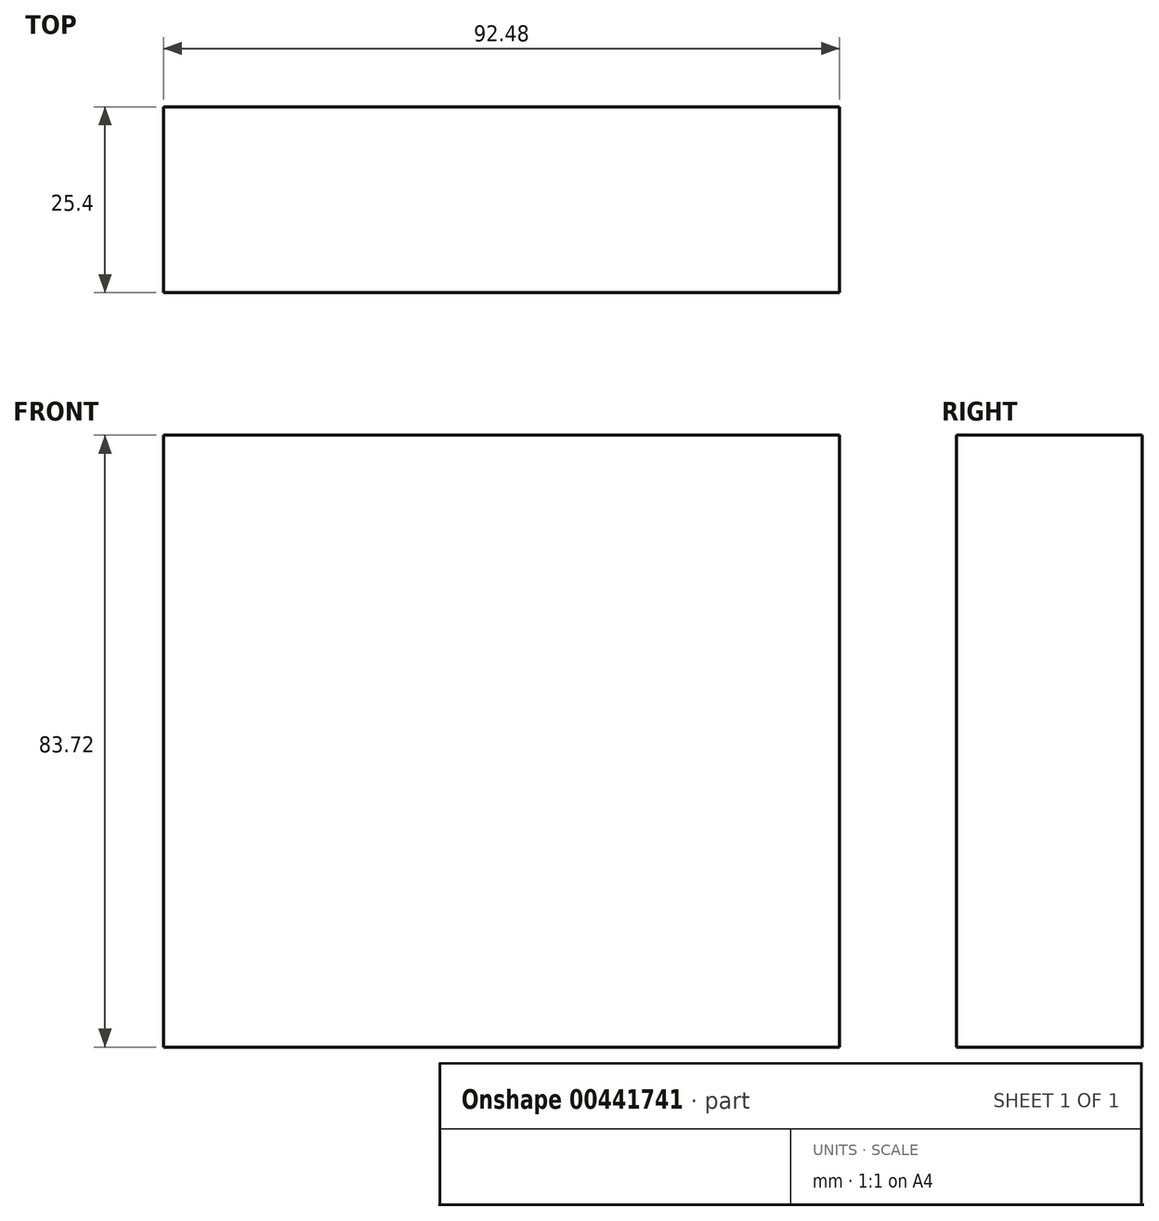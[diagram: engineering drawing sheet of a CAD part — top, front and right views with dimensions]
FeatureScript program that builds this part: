
annotation { "Feature Type Name" : "Feature", "Feature Type Description" : "" }
export const myFeature = defineFeature(function(context is Context, id is Id, definition is map)
    precondition{}
    {
        {
            var Q0;
            Q0=qCreatedBy(makeId("Front.planeOp"),FACE);
            var sketch = newSketch(context, id + "F0", { "sketchPlane" : qUnion([Q0])});
            skLineSegment(sketch, "E0.bottom", {"start": v(-46.24, -41.86) * mm, "end": v(46.24, -41.86) * mm});
            skLineSegment(sketch, "E0.top", {"start": v(-46.24, 41.86) * mm, "end": v(46.24, 41.86) * mm});
            skLineSegment(sketch, "E0.left", {"start": v(-46.24, -41.86) * mm, "end": v(-46.24, 41.86) * mm});
            skLineSegment(sketch, "E0.right", {"start": v(46.24, -41.86) * mm, "end": v(46.24, 41.86) * mm});
            skPoint(sketch, "E0.middle", {"position": v(0, 0) * mm});
            skSolve(sketch);
        }
        {
            var Q0;
            Q0 = qSketchRegion(id + "F0", true);
            extrude(context, id + "F1", {"entities" : qUnion([Q0]), "endBound" : BoundingType.SYMMETRIC, "depth" : 25.4 * mm});
        }
    });
